# Revit family: MIA12_63_UN_Downlighter_ETK
name_source: partatom
category: Lighting Fixtures
revit_build: Autodesk Revit 2017 (Build: 20190508_0315(x64)
units: mm (PartAtom-declared; Revit-internal decimal feet)

## family parameters
Always vertical = Yes
Cut with Voids When Loaded = No
Light Source = No
OmniClass Number = 23.80.70.11.14.11
OmniClass Title = Downlights
Part Type = Normal
Room Calculation Point = Yes
Round Connector Dimension = Use Diameter
Shared = No
Work Plane-Based = No

## types (8) — shared parameters
Apparent Load = 10 VA
Assembly Code = 63.0
Bundle = 110°
Calc_Radius_housing = 80 mm  [stored 0.262467 ft]
Diameter = 180 mm  [stored 0.590551 ft]
IfcExportAs = IfcLightFixtureType
IfcExportType = USERDEFINED
Lamp = LED
Light Source = MIA.1 - Lightsource : ALL.1100.15 - 15W / 1500lm / 3000K
Manufacturer = ETK licht B.V.
Model = MIA.1
Radius = 90 mm  [stored 0.295276 ft]
Type Comments = IP40
URL = http://www.etk.nl
Voltage = 230 V
Wattage Comments = 10W

## per-type parameters (varying)
| type | Luminaire_Material |
| MIA.1210.15 - Ø180 / 10W / 1000lm / 3000K | RAL9003 |
| MIA.1210.25/35 - Ø180 / 10W / 1000lm / 3000K | RAL9005 |
| MIA.1260.15 - Ø180 / 10W / 1100lm / 4000K | RAL9003 |
| MIA.1260.25/35 - Ø180 / 10W / 1100lm / 4000K | RAL9005 |
| MIA.1213.15 - Ø180 / 10W / 1000lm / 3000K | RAL9003 |
| MIA.1213.25/35 - Ø180 / 10W / 1000lm / 3000K | RAL9005 |
| MIA.1263.15 - Ø180 / 10W / 1100lm / 4000K | RAL9003 |
| MIA.1263.25/35 - Ø180 / 10W / 1100lm / 4000K | RAL9005 |

note: [stored X ft] marks values corroborated as IEEE doubles in the binary element streams (Revit-internal decimal feet)

## geometry (parser evidence)
native form markers: Sweep x6
no freeform markers — native parametric forms only
